# Revit family: Thorn ALTIS GEN5 Gearbox-Performance-class C3 without NTC
name_source: partatom
category: Electrical Fixtures
units: mm (PartAtom-declared; Revit-internal decimal feet)

## family parameters
Cut with Voids When Loaded = Yes
Host = Face
Maintain Annotation Orientation = No
Part Type = Normal
Room Calculation Point = Yes
Round Connector Dimension = Use Diameter
Shared = Yes

## types (8) — shared parameters
Apparent Load = 2100 VA
Assembly Code = Pr_60_70_48_54
Description = LED Control Gear
Export Type to IFC As = IfcLightFixtureType
Lamp = LED
Luminaire Height = 77 mm  [stored 0.252625 ft]
Luminaire Length = 500 mm  [stored 1.64042 ft]
Luminaire Width = 152 mm  [stored 0.498688 ft]
Manufacturer = Thorn Lighting
Material Housing = Thorn-Aluminium-RAL 7043-Traffic Grey B
Power Factor = 1
Type IFC Predefined Type = DIRECTIONSOURCE
Type Image = TLG_ALG5_F_GB_LE_2100W.jpg
URL = https://www.thornlighting.com
Wattage = 2100 W
zero-valued in all types: Default Elevation

## per-type parameters (varying)
| type | Model |
| ALG5 GB LE 2100W 0.85A 550V 3CH DA | 96684149 |
| ALG5 GB LE 2100W 0.85A 550V 3CH RDMX | 96684152 |
| ALG5 GB LE 2100W 1.05A 550V 3CH DA | 96684148 |
| ALG5 GB LE 2100W 1.05A 550V 3CH RDMX | 96684151 |
| ALG5 GB LE 2100W 1.25A 550V 3CH DA | 96688776 |
| ALG5 GB LE 2100W 1.25A 550V 3CH RDMX | 96688777 |
| ALG5 GB LE 2100W 1.40A 550V 3CH DA | 96684147 |
| ALG5 GB LE 2100W 1.40A 550V 3CH RDMX | 96684150 |

note: [stored X ft] marks values corroborated as IEEE doubles in the binary element streams (Revit-internal decimal feet)

## geometry (parser evidence)
native form markers: Sweep x2
no freeform markers — native parametric forms only
